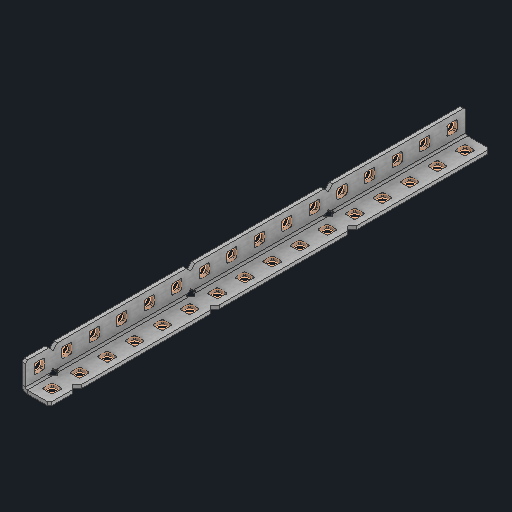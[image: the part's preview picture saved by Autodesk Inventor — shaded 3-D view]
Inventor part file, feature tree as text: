
AUTODESK INVENTOR PART (.ipt)
format: ipt  version: 2025 (Build 290162000, 162)  size: 754,688 bytes
history: native  units: in
note: dims shown in document units (in); Inventor stores cm internally (conversion verified against a paired STEP export)
features: other x73, sketch x2, sheet_metal_op x1
ambient origin geometry x8: Origin, YZ Plane, XZ Plane, XY Plane, X Axis, Y Axis, Z Axis, Center Point
bodies: Solid1 (feature_tree)
feature tree (76):
  other  "Alu Angle 1x1x16.ipt"
  other  "Solid1::Alu Angle 1x1x16.ipt"
  other  "TaggingFeature1"
  sketch  "Sketch1"  dims[d0=0.3937in]
  sketch  "Sketch2"  dims[d1=0.0625in]
  sheet_metal_op  "Body Pattern Sketch"
  other  "Arc Length"
  other  "Diagonal Plane"
  other  "Srf1"
  other  "Srf2"
  other  "Srf3"
  other  "Srf4"
  other  "Srf5"
  other  "Srf6"
  other  "Srf7"
  other  "Srf8"
  other  "Srf9"
  other  "Srf10"
  other  "Srf11"
  other  "Srf12"
  other  "Srf13"
  other  "Srf14"
  other  "Srf15"
  other  "Srf16"
  other  "Srf17"
  other  "Srf18"
  other  "Srf19"
  other  "Srf20"
  other  "Srf21"
  other  "Srf22"
  other  "Srf23"
  other  "Srf24"
  other  "Srf25"
  other  "Srf26"
  other  "Srf27"
  other  "Srf28"
  other  "Srf29"
  other  "Srf30"
  other  "Srf31"
  other  "Srf32"
  other  "Srf33"
  other  "Srf34"
  other  "Srf91::Derived"
  other  "Srf92::Derived"
  other  "Srf856::Derived"
  other  "Srf857::Derived"
  other  "Srf858::Derived"
  other  "Srf859::Derived"
  other  "Srf860::Derived"
  other  "Srf861::Derived"
  other  "Srf1383::Derived"
  other  "Srf1384::Derived"
  other  "Srf1385::Derived"
  other  "Srf1386::Derived"
  other  "Srf1387::Derived"
  other  "Srf1388::Derived"
  other  "Srf1389::Derived"
  other  "Srf1390::Derived"
  other  "Srf1391::Derived"
  other  "Srf1275::Derived"
  other  "Srf1276::Derived"
  other  "Srf1278::Derived"
  other  "Srf1279::Derived"
  other  "Srf1280::Derived"
  other  "Srf1281::Derived"
  other  "Srf1282::Derived"
  other  "Srf1283::Derived"
  other  "Srf1475::Derived"
  other  "Srf1476::Derived"
  other  "Srf1477::Derived"
  other  "Srf1478::Derived"
  other  "Srf1479::Derived"
  other  "Srf1480::Derived"
  other  "Srf1481::Derived"
  other  "Srf1482::Derived"
  other  "Srf1483::Derived"
